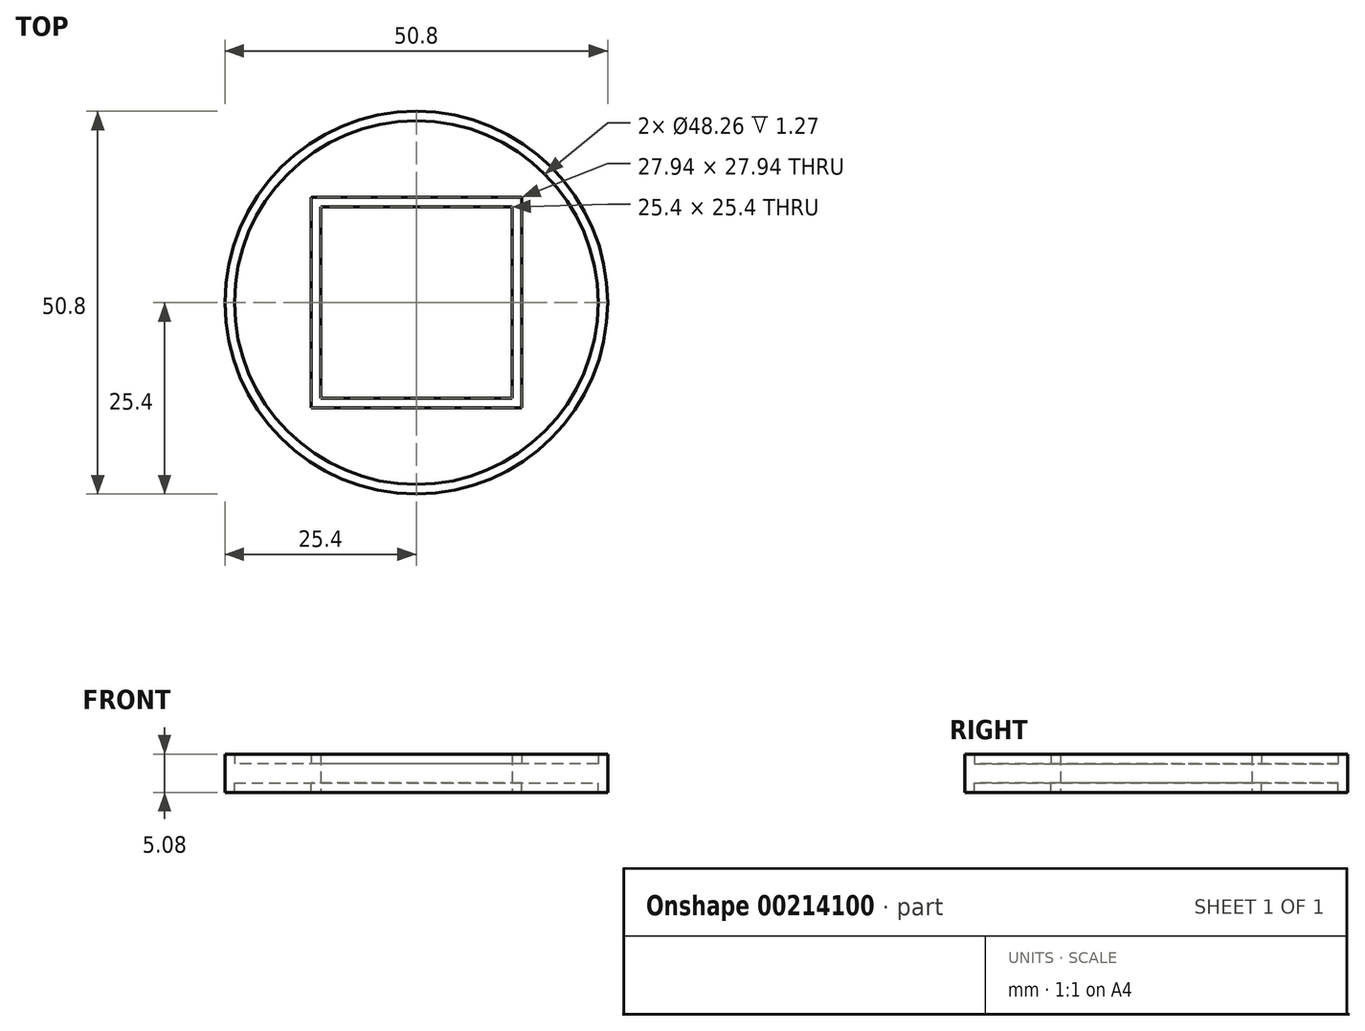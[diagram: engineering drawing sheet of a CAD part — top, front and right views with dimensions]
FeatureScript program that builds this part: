
annotation { "Feature Type Name" : "Feature", "Feature Type Description" : "" }
export const myFeature = defineFeature(function(context is Context, id is Id, definition is map)
    precondition{}
    {
        {
            var Q0;
            Q0=qCreatedBy(makeId("Top.planeOp"),FACE);
            var sketch = newSketch(context, id + "F0", { "sketchPlane" : qUnion([Q0])});
            skCircle(sketch, "E0", {"center": v(0, 0) * mm, "radius": 25.4 * mm});
            skLineSegment(sketch, "E1.bottom", {"start": v(12.7, -12.7) * mm, "end": v(-12.7, -12.7) * mm});
            skLineSegment(sketch, "E1.top", {"start": v(12.7, 12.7) * mm, "end": v(-12.7, 12.7) * mm});
            skLineSegment(sketch, "E1.left", {"start": v(12.7, -12.7) * mm, "end": v(12.7, 12.7) * mm});
            skLineSegment(sketch, "E1.right", {"start": v(-12.7, -12.7) * mm, "end": v(-12.7, 12.7) * mm});
            skSolve(sketch);
        }
        {
            var Q0;
            Q0=makeQuery(id+"F0.imprint","IMPRINT",FACE,{"disambiguationData":[TD([[makeQuery(id+"F0.imprint","IMPRINT",EDGE,{"derivedFrom":sQuery(id+"F0.wireOp",EDGE,"E0")}),1.0]])]});
            extrude(context, id + "F1", {"entities" : qUnion([Q0]), "depth" : 2.54 * mm});
        }
        {
            var Q0;
            Q0=makeQuery(id+"F1.opExtrude","CAP_FACE",FACE,{"disambiguationData":[OSD([sQuery(id+"F0.wireOp",EDGE,"E0"),sQuery(id+"F0.wireOp",EDGE,"E1.bottom"),sQuery(id+"F0.wireOp",EDGE,"E1.top"),sQuery(id+"F0.wireOp",EDGE,"E1.left"),sQuery(id+"F0.wireOp",EDGE,"E1.right")])],"isStart":false});
            var sketch = newSketch(context, id + "F2", { "sketchPlane" : qUnion([Q0])});
            skLineSegment(sketch, "E2.bottom", {"start": v(13.97, -13.97) * mm, "end": v(-13.97, -13.97) * mm});
            skLineSegment(sketch, "E2.top", {"start": v(13.97, 13.97) * mm, "end": v(-13.97, 13.97) * mm});
            skLineSegment(sketch, "E2.left", {"start": v(13.97, -13.97) * mm, "end": v(13.97, 13.97) * mm});
            skLineSegment(sketch, "E2.right", {"start": v(-13.97, -13.97) * mm, "end": v(-13.97, 13.97) * mm});
            skPoint(sketch, "E2.middle", {"position": v(0, 0) * mm});
            skCircle(sketch, "E3", {"center": v(0, 0) * mm, "radius": 24.13 * mm});
            skSolve(sketch);
        }
        {
            var Q0;
            Q0=makeQuery(id+"F2.imprint","IMPRINT",FACE,{"disambiguationData":[TD([[makeQuery(id+"F2.imprint","IMPRINT",EDGE,{"derivedFrom":sQuery(id+"F2.wireOp",EDGE,"E2.bottom")}),-1.0]])]});
            var Q1;
            Q1=makeQuery(id+"F2.imprint","IMPRINT",FACE,{"disambiguationData":[TD([[makeQuery(id+"F2.imprint","IMPRINT",EDGE,{"derivedFrom":sQuery(id+"F2.wireOp",EDGE,"E3")}),-1.0]])]});
            extrude(context, id + "F3", {"entities" : qUnion([Q0, Q1]), "operationType" : NewBodyOperationType.ADD, "depth" : 1.27 * mm});
        }
        {
            var Q0;
            Q0=makeQuery(id+"F1.opExtrude","CAP_FACE",FACE,{"disambiguationData":[OSD([sQuery(id+"F0.wireOp",EDGE,"E0"),sQuery(id+"F0.wireOp",EDGE,"E1.bottom"),sQuery(id+"F0.wireOp",EDGE,"E1.top"),sQuery(id+"F0.wireOp",EDGE,"E1.left"),sQuery(id+"F0.wireOp",EDGE,"E1.right")])],"isStart":true});
            var sketch = newSketch(context, id + "F4", { "sketchPlane" : qUnion([Q0])});
            skCircle(sketch, "E4", {"center": v(0, 0) * mm, "radius": 24.13 * mm});
            skLineSegment(sketch, "E5.bottom", {"start": v(13.97, -13.97) * mm, "end": v(-13.97, -13.97) * mm});
            skLineSegment(sketch, "E5.top", {"start": v(13.97, 13.97) * mm, "end": v(-13.97, 13.97) * mm});
            skLineSegment(sketch, "E5.left", {"start": v(13.97, -13.97) * mm, "end": v(13.97, 13.97) * mm});
            skLineSegment(sketch, "E5.right", {"start": v(-13.97, -13.97) * mm, "end": v(-13.97, 13.97) * mm});
            skSolve(sketch);
        }
        {
            var Q0;
            Q0=makeQuery(id+"F4.imprint","IMPRINT",FACE,{"disambiguationData":[TD([[makeQuery(id+"F4.imprint","IMPRINT",EDGE,{"derivedFrom":sQuery(id+"F4.wireOp",EDGE,"E4")}),-1.0]])]});
            var Q1;
            Q1=makeQuery(id+"F4.imprint","IMPRINT",FACE,{"disambiguationData":[TD([[makeQuery(id+"F4.imprint","IMPRINT",EDGE,{"derivedFrom":sQuery(id+"F4.wireOp",EDGE,"E5.bottom")}),-1.0]])]});
            extrude(context, id + "F5", {"entities" : qUnion([Q0, Q1]), "operationType" : NewBodyOperationType.ADD, "depth" : 1.27 * mm});
        }
    });
